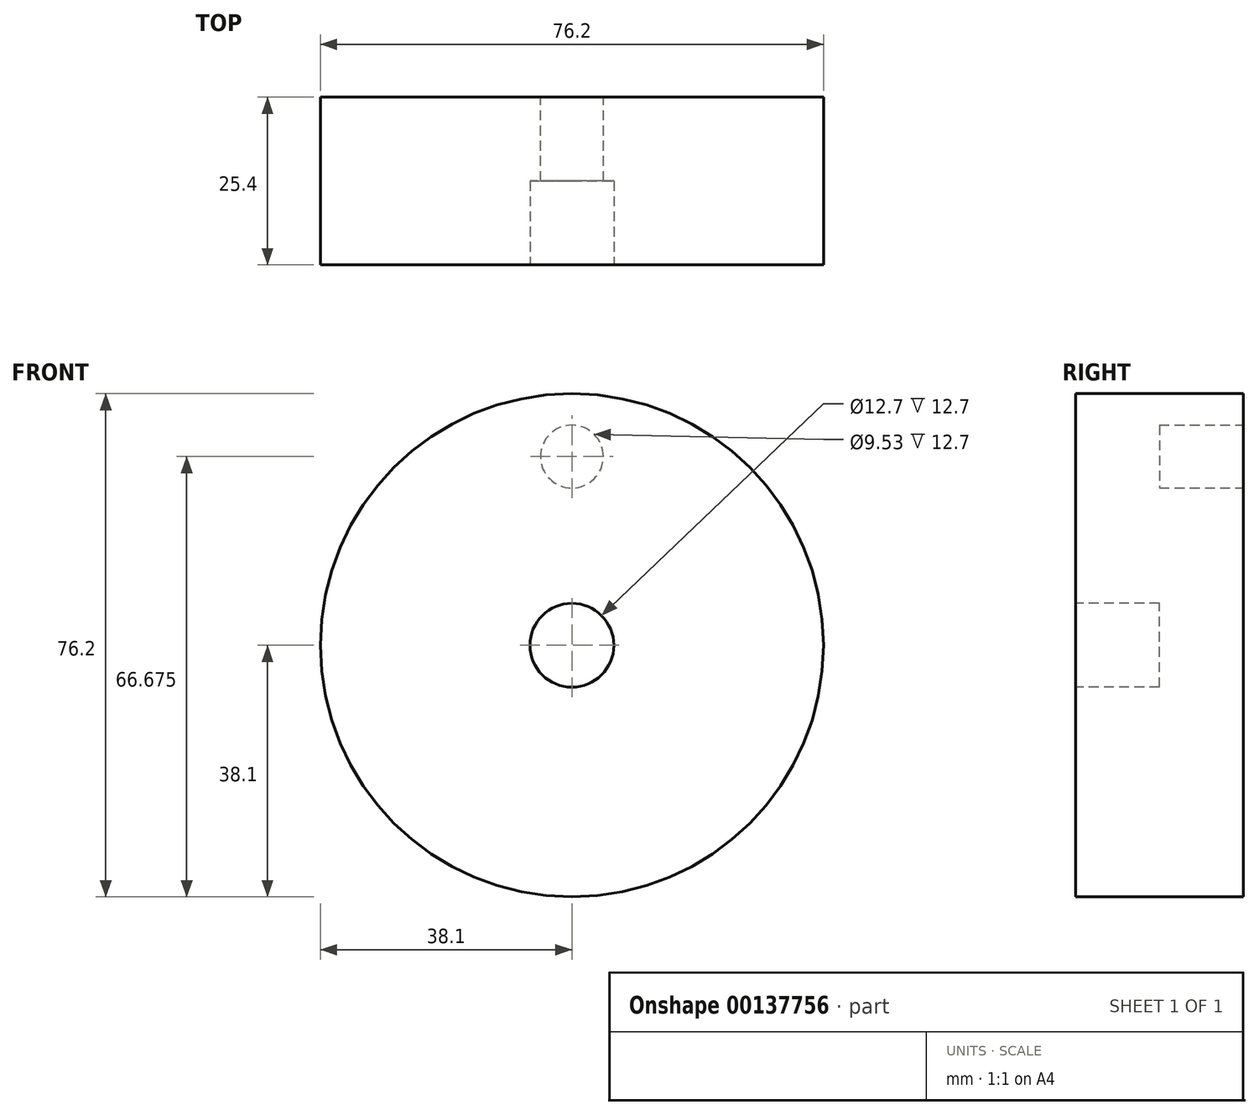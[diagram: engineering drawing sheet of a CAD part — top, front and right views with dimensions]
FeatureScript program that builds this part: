
annotation { "Feature Type Name" : "Feature", "Feature Type Description" : "" }
export const myFeature = defineFeature(function(context is Context, id is Id, definition is map)
    precondition{}
    {
        {
            var Q0;
            Q0=qCreatedBy(makeId("Front.planeOp"),FACE);
            var sketch = newSketch(context, id + "F0", { "sketchPlane" : qUnion([Q0])});
            skCircle(sketch, "E0", {"center": v(0, 0) * mm, "radius": 38.1 * mm});
            skSolve(sketch);
        }
        {
            var Q0;
            Q0=makeQuery(id+"F0.imprint","IMPRINT",FACE,{"disambiguationData":[TD([[makeQuery(id+"F0.imprint","IMPRINT",EDGE,{"derivedFrom":sQuery(id+"F0.wireOp",EDGE,"E0")}),1.0]])]});
            extrude(context, id + "F1", {"entities" : qUnion([Q0]), "depth" : 25.4 * mm});
        }
        {
            var Q0;
            Q0=makeQuery(id+"F1.opExtrude","CAP_FACE",FACE,{"disambiguationData":[OSD([sQuery(id+"F0.wireOp",EDGE,"E0")])],"isStart":false});
            var sketch = newSketch(context, id + "F2", { "sketchPlane" : qUnion([Q0])});
            skCircle(sketch, "E1", {"center": v(0, 0) * mm, "radius": 6.35 * mm});
            skSolve(sketch);
        }
        {
            var Q0;
            Q0 = qSketchRegion(id + "F2", true);
            var Q1;
            Q1=qCreatedBy(makeId("Right.planeOp"),FACE);
            extrude(context, id + "F3", {"entities" : qUnion([Q0]), "operationType" : NewBodyOperationType.REMOVE, "oppositeDirection" : true, "endBoundEntityFace" : qUnion([Q1]), "depth" : 12.7 * mm});
        }
        {
            var Q0;
            Q0=makeQuery(id+"F1.opExtrude","CAP_FACE",FACE,{"disambiguationData":[OSD([sQuery(id+"F0.wireOp",EDGE,"E0")])],"isStart":true});
            var sketch = newSketch(context, id + "F4", { "sketchPlane" : qUnion([Q0])});
            skCircle(sketch, "E2", {"center": v(0, 28.58) * mm, "radius": 4.76 * mm});
            skSolve(sketch);
        }
        {
            var Q0;
            Q0 = qSketchRegion(id + "F4", true);
            extrude(context, id + "F5", {"entities" : qUnion([Q0]), "operationType" : NewBodyOperationType.REMOVE, "oppositeDirection" : true, "depth" : 12.7 * mm});
        }
    });
